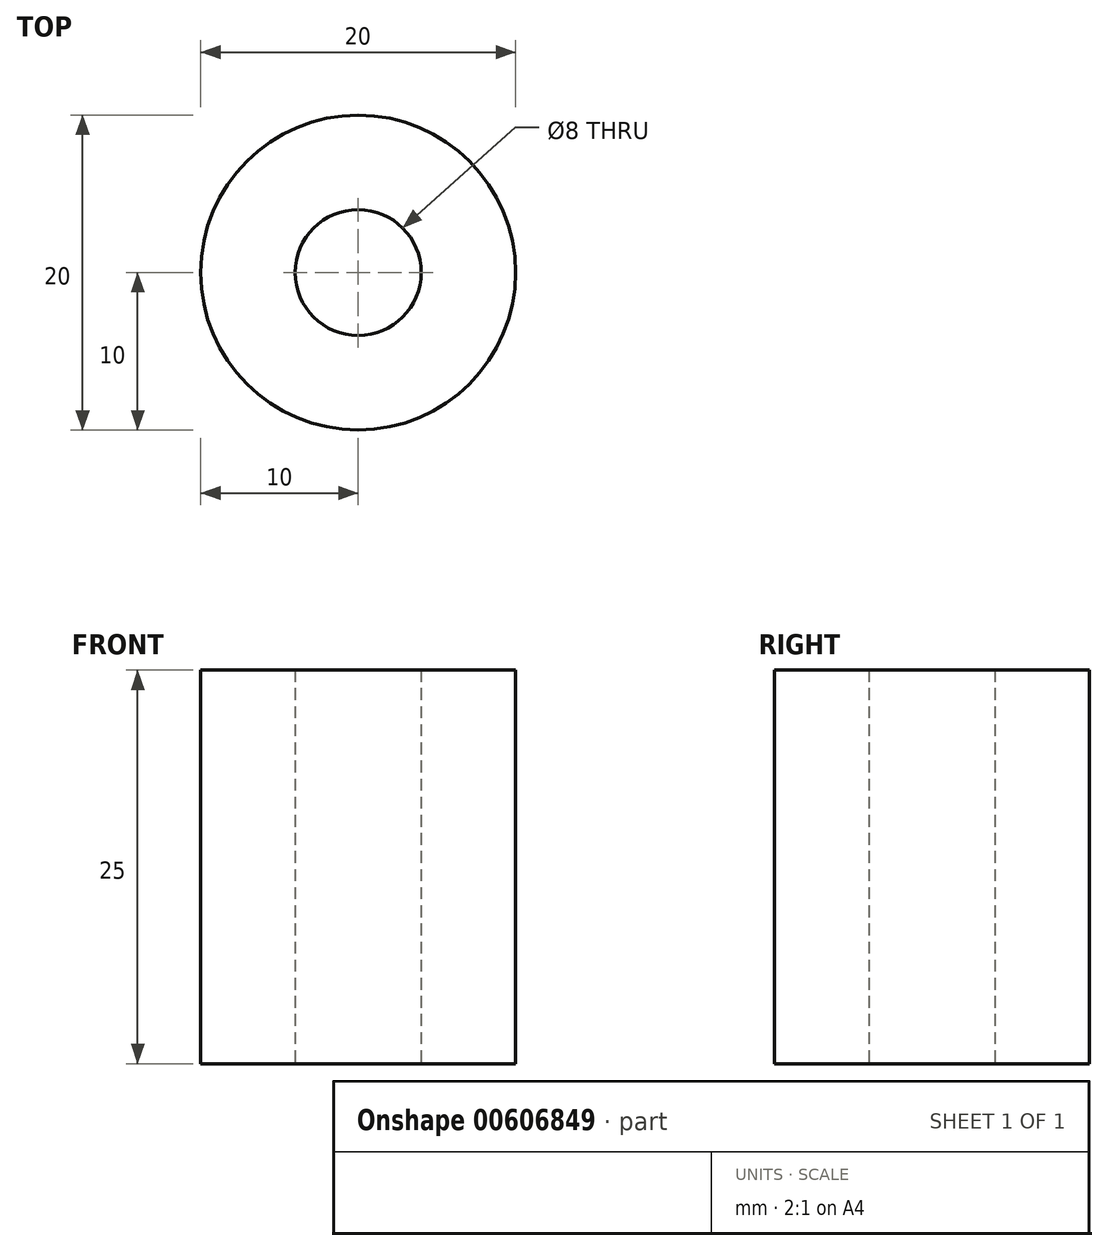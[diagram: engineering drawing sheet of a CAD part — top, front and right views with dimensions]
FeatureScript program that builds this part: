
annotation { "Feature Type Name" : "Feature", "Feature Type Description" : "" }
export const myFeature = defineFeature(function(context is Context, id is Id, definition is map)
    precondition{}
    {
        {
            var Q0;
            Q0=qCreatedBy(makeId("Top.planeOp"),FACE);
            var sketch = newSketch(context, id + "F0", { "sketchPlane" : qUnion([Q0])});
            skCircle(sketch, "E0", {"center": v(0, 0) * mm, "radius": 3 * mm});
            skCircle(sketch, "E1", {"center": v(0, 0) * mm, "radius": 4 * mm});
            skCircle(sketch, "E2", {"center": v(0, 0) * mm, "radius": 10 * mm});
            skCircle(sketch, "E3", {"center": v(-46.07, 0) * mm, "radius": 3 * mm});
            skCircle(sketch, "E4", {"center": v(-46.07, 0) * mm, "radius": 10 * mm});
            skSolve(sketch);
        }
        {
            var Q0;
            Q0=makeQuery(id+"F0.imprint","IMPRINT",FACE,{"disambiguationData":[TD([[makeQuery(id+"F0.imprint","IMPRINT",EDGE,{"derivedFrom":sQuery(id+"F0.wireOp",EDGE,"E1")}),-1.0]])]});
            extrude(context, id + "F1", {"entities" : qUnion([Q0]), "depth" : 25 * mm, "offsetDistance" : 25 * mm});
        }
    });
